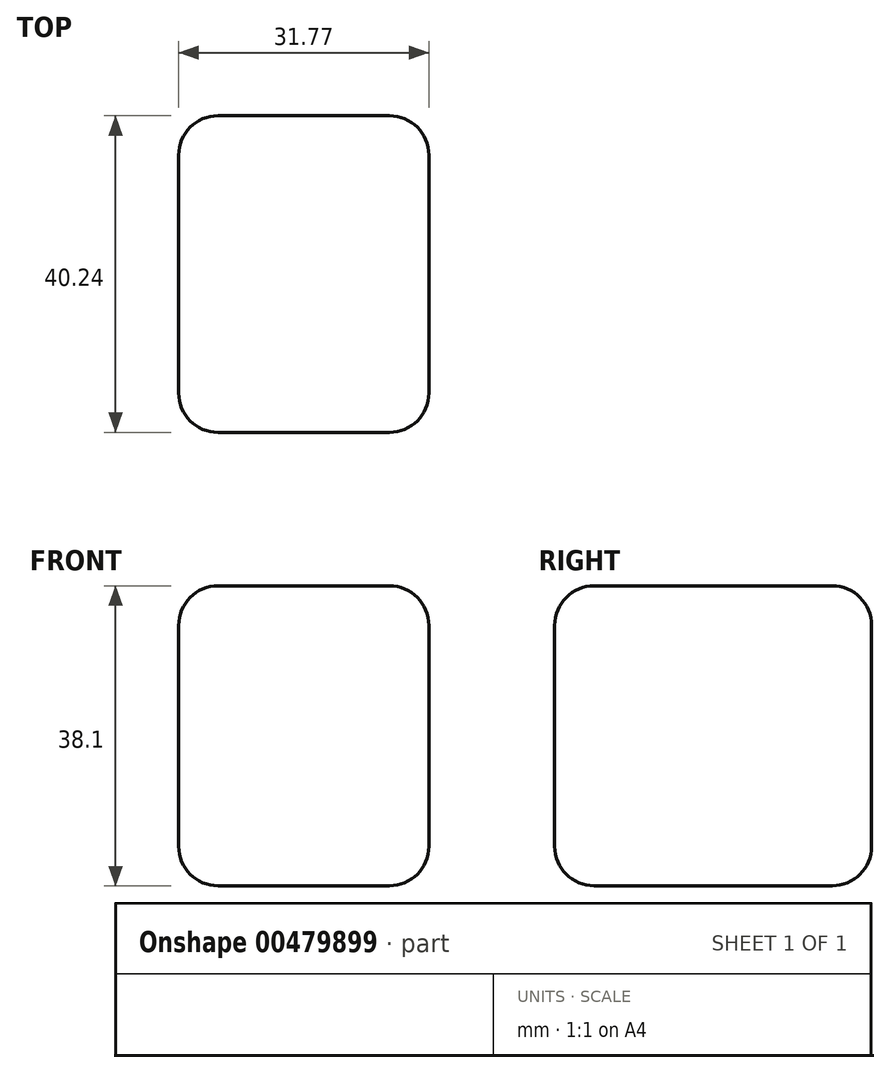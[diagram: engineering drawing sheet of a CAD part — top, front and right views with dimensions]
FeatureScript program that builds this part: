
annotation { "Feature Type Name" : "Feature", "Feature Type Description" : "" }
export const myFeature = defineFeature(function(context is Context, id is Id, definition is map)
    precondition{}
    {
        {
            var Q0;
            Q0=qCreatedBy(makeId("Top.planeOp"),FACE);
            var sketch = newSketch(context, id + "F0", { "sketchPlane" : qUnion([Q0])});
            skLineSegment(sketch, "E0", {"start": v(-35.85, 38.62) * mm, "end": v(-17.78, 20.55) * mm});
            skLineSegment(sketch, "E1", {"start": v(-19.1, 21.86) * mm, "end": v(-37.9, 3.06) * mm});
            skLineSegment(sketch, "E2", {"start": v(-37.9, 3.06) * mm, "end": v(-55.38, 20.55) * mm});
            skLineSegment(sketch, "E3", {"start": v(-55.38, 20.55) * mm, "end": v(-35.85, 38.62) * mm});
            skLineSegment(sketch, "E4", {"start": v(-17.78, 20.55) * mm, "end": v(-19.1, 21.86) * mm});
            skLineSegment(sketch, "E5", {"start": v(0, 0) * mm, "end": v(31.77, 0) * mm});
            skLineSegment(sketch, "E6", {"start": v(31.77, 0) * mm, "end": v(31.77, -27.54) * mm});
            skLineSegment(sketch, "E7", {"start": v(31.77, -27.54) * mm, "end": v(0, -27.54) * mm});
            skLineSegment(sketch, "E8", {"start": v(0, -27.54) * mm, "end": v(0, 0) * mm});
            skSolve(sketch);
        }
        {
            var Q0;
            Q0=makeQuery(id+"F0.imprint","IMPRINT",FACE,{"disambiguationData":[TD([[makeQuery(id+"F0.imprint","IMPRINT",EDGE,{"derivedFrom":sQuery(id+"F0.wireOp",EDGE,"E5")}),-1.0]])]});
            extrude(context, id + "F1", {"entities" : qUnion([Q0]), "depth" : 38.1 * mm});
        }
        {
            var Q0;
            Q0=makeQuery(id+"F1.opExtrude","SWEPT_FACE",FACE,{"disambiguationData":[OSD([sQuery(id+"F0.wireOp",EDGE,"E7")])]});
            extrude(context, id + "F2", {"entities" : qUnion([Q0]), "operationType" : NewBodyOperationType.ADD, "depth" : 12.7 * mm});
        }
        {
            var Q0;
            Q0=makeQuery(id+"F2.opExtrude","CAP_EDGE",EDGE,{"disambiguationData":[OSD([sQuery(id+"F0.wireOp",EDGE,"E7"),sQuery(id+"F0.wireOp",EDGE,"E8")])],"isStart":false});
            var Q1;
            {var subQ0=sQuery(id+"F0.wireOp",EDGE,"E8");var subQ1=sQuery(id+"F0.wireOp",EDGE,"E7");Q1=makeQuery(id+"F2.boolean.opBoolean","MERGE",EDGE,{"derivedFrom":[makeQuery(id+"F1.opExtrude","CAP_EDGE",EDGE,{"disambiguationData":[OSD([subQ0])],"isStart":false}),makeQuery(id+"F2.opExtrude","SWEPT_EDGE",EDGE,{"disambiguationData":[OSD([subQ1,subQ0]),TDD([makeQuery(id+"F1.opExtrude","CAP_VERTEX",VERTEX,{"disambiguationData":[OSD([subQ1,subQ0])],"isStart":false})])]})]});}
            var Q2;
            {var subQ0=sQuery(id+"F0.wireOp",EDGE,"E7");var subQ1=sQuery(id+"F0.wireOp",EDGE,"E6");Q2=makeQuery(id+"F2.boolean.opBoolean","MERGE",EDGE,{"derivedFrom":[makeQuery(id+"F1.opExtrude","CAP_EDGE",EDGE,{"disambiguationData":[OSD([subQ1])],"isStart":true}),makeQuery(id+"F2.opExtrude","SWEPT_EDGE",EDGE,{"disambiguationData":[OSD([subQ1,subQ0]),TDD([makeQuery(id+"F1.opExtrude","CAP_VERTEX",VERTEX,{"disambiguationData":[OSD([subQ1,subQ0])],"isStart":true})])]})]});}
            var Q3;
            {var subQ0=sQuery(id+"F0.wireOp",EDGE,"E7");var subQ1=sQuery(id+"F0.wireOp",EDGE,"E6");Q3=makeQuery(id+"F2.boolean.opBoolean","MERGE",EDGE,{"derivedFrom":[makeQuery(id+"F1.opExtrude","CAP_EDGE",EDGE,{"disambiguationData":[OSD([subQ1])],"isStart":false}),makeQuery(id+"F2.opExtrude","SWEPT_EDGE",EDGE,{"disambiguationData":[OSD([subQ1,subQ0]),TDD([makeQuery(id+"F1.opExtrude","CAP_VERTEX",VERTEX,{"disambiguationData":[OSD([subQ1,subQ0])],"isStart":false})])]})]});}
            var Q4;
            Q4=makeQuery(id+"F2.opExtrude","CAP_EDGE",EDGE,{"disambiguationData":[OSD([sQuery(id+"F0.wireOp",EDGE,"E6"),sQuery(id+"F0.wireOp",EDGE,"E7")])],"isStart":false});
            var Q5;
            Q5=makeQuery(id+"F1.opExtrude","CAP_EDGE",EDGE,{"disambiguationData":[OSD([sQuery(id+"F0.wireOp",EDGE,"E5")])],"isStart":false});
            var Q6;
            {var subQ0=sQuery(id+"F0.wireOp",EDGE,"E7");Q6=makeQuery(id+"F2.opExtrude","CAP_EDGE",EDGE,{"disambiguationData":[OSD([subQ0]),TDD([makeQuery(id+"F1.opExtrude","CAP_EDGE",EDGE,{"disambiguationData":[OSD([subQ0])],"isStart":true})])],"isStart":false});}
            var Q7;
            {var subQ0=sQuery(id+"F0.wireOp",EDGE,"E8");var subQ1=sQuery(id+"F0.wireOp",EDGE,"E7");Q7=makeQuery(id+"F2.boolean.opBoolean","MERGE",EDGE,{"derivedFrom":[makeQuery(id+"F1.opExtrude","CAP_EDGE",EDGE,{"disambiguationData":[OSD([subQ0])],"isStart":true}),makeQuery(id+"F2.opExtrude","SWEPT_EDGE",EDGE,{"disambiguationData":[OSD([subQ1,subQ0]),TDD([makeQuery(id+"F1.opExtrude","CAP_VERTEX",VERTEX,{"disambiguationData":[OSD([subQ1,subQ0])],"isStart":true})])]})]});}
            var Q8;
            {var subQ0=sQuery(id+"F0.wireOp",EDGE,"E7");Q8=makeQuery(id+"F2.opExtrude","CAP_EDGE",EDGE,{"disambiguationData":[OSD([subQ0]),TDD([makeQuery(id+"F1.opExtrude","CAP_EDGE",EDGE,{"disambiguationData":[OSD([subQ0])],"isStart":false})])],"isStart":false});}
            var Q9;
            Q9=makeQuery(id+"F1.opExtrude","CAP_EDGE",EDGE,{"disambiguationData":[OSD([sQuery(id+"F0.wireOp",EDGE,"E5")])],"isStart":true});
            var Q10;
            Q10=makeQuery(id+"F1.opExtrude","SWEPT_EDGE",EDGE,{"disambiguationData":[OSD([sQuery(id+"F0.wireOp",EDGE,"E5"),sQuery(id+"F0.wireOp",EDGE,"E8")])]});
            fillet(context, id + "F3", {"entities" : qUnion([Q0, Q1, Q2, Q3, Q4, Q5, Q6, Q7, Q8, Q9, Q10]), "radius" : 5 * mm, "tangentPropagation" : true, "allowEdgeOverflow" : false});
        }
        {
            var Q0;
            Q0=makeQuery(id+"F1.opExtrude","SWEPT_EDGE",EDGE,{"disambiguationData":[OSD([sQuery(id+"F0.wireOp",EDGE,"E5"),sQuery(id+"F0.wireOp",EDGE,"E6")])]});
            fillet(context, id + "F4", {"entities" : qUnion([Q0]), "radius" : 5 * mm, "tangentPropagation" : true, "allowEdgeOverflow" : false});
        }
    });
